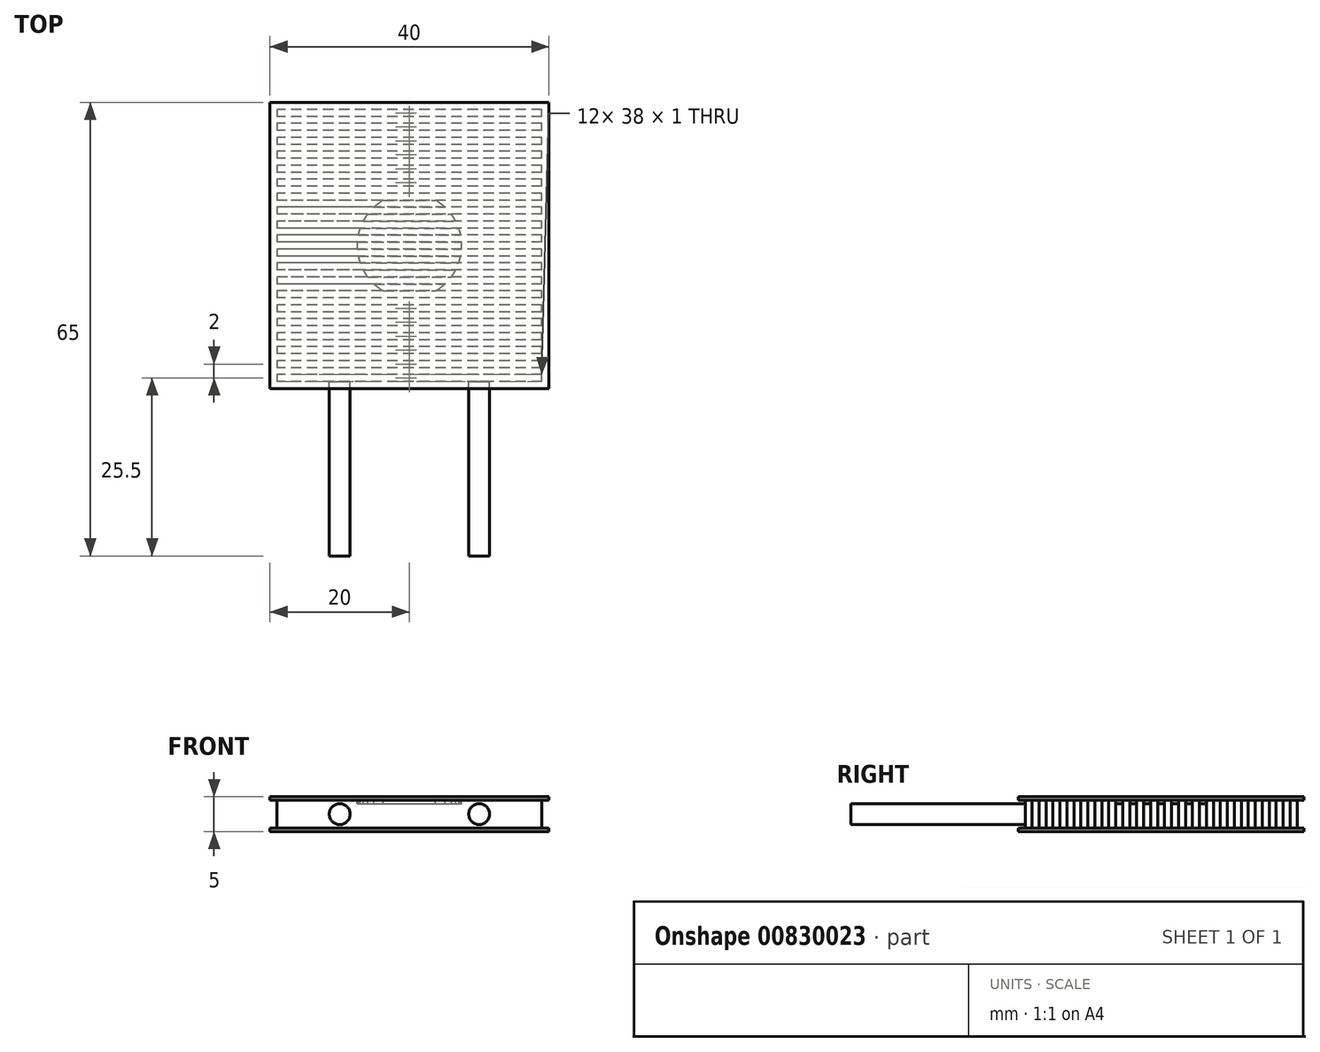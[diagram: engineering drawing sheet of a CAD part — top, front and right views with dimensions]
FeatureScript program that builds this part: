
annotation { "Feature Type Name" : "Feature", "Feature Type Description" : "" }
export const myFeature = defineFeature(function(context is Context, id is Id, definition is map)
    precondition{}
    {
        {
            var Q0;
            Q0=qCreatedBy(makeId("Top.planeOp"),FACE);
            var sketch = newSketch(context, id + "F0", { "sketchPlane" : qUnion([Q0])});
            skLineSegment(sketch, "E0.bottom", {"start": v(0, 0) * mm, "end": v(40, 0) * mm});
            skLineSegment(sketch, "E0.top", {"start": v(0, -41) * mm, "end": v(40, -41) * mm});
            skLineSegment(sketch, "E0.left", {"start": v(0, 0) * mm, "end": v(0, -41) * mm});
            skLineSegment(sketch, "E0.right", {"start": v(40, 0) * mm, "end": v(40, -41) * mm});
            skSolve(sketch);
        }
        {
            var Q0;
            Q0=makeQuery(id+"F0.imprint","IMPRINT",FACE,{"disambiguationData":[TD([[makeQuery(id+"F0.imprint","IMPRINT",EDGE,{"derivedFrom":sQuery(id+"F0.wireOp",EDGE,"E0.bottom")}),-1.0]])]});
            extrude(context, id + "F1", {"entities" : qUnion([Q0]), "depth" : 5 * mm, "offsetDistance" : 25 * mm});
        }
        {
            var Q0;
            Q0=makeQuery(id+"F1.opExtrude","SWEPT_FACE",FACE,{"disambiguationData":[OSD([sQuery(id+"F0.wireOp",EDGE,"E0.left")])]});
            var sketch = newSketch(context, id + "F2", { "sketchPlane" : qUnion([Q0])});
            skLineSegment(sketch, "E1.bottom", {"start": v(0, 4.5) * mm, "end": v(1, 4.5) * mm});
            skLineSegment(sketch, "E1.top", {"start": v(0, 0.5) * mm, "end": v(1, 0.5) * mm});
            skLineSegment(sketch, "E1.left", {"start": v(0, 4.5) * mm, "end": v(0, 0.5) * mm});
            skLineSegment(sketch, "E1.right", {"start": v(1, 4.5) * mm, "end": v(1, 0.5) * mm});
            skLineSegment(sketch, "E2.1.0.0", {"start": v(3, 4.5) * mm, "end": v(3, 0.5) * mm});
            skLineSegment(sketch, "E2.1.0.1", {"start": v(2, 4.5) * mm, "end": v(2, 0.5) * mm});
            skLineSegment(sketch, "E2.1.0.2", {"start": v(2, 4.5) * mm, "end": v(3, 4.5) * mm});
            skLineSegment(sketch, "E2.1.0.3", {"start": v(2, 0.5) * mm, "end": v(3, 0.5) * mm});
            skLineSegment(sketch, "E2.2.0.0", {"start": v(5, 4.5) * mm, "end": v(5, 0.5) * mm});
            skLineSegment(sketch, "E2.2.0.1", {"start": v(4, 4.5) * mm, "end": v(4, 0.5) * mm});
            skLineSegment(sketch, "E2.2.0.2", {"start": v(4, 4.5) * mm, "end": v(5, 4.5) * mm});
            skLineSegment(sketch, "E2.2.0.3", {"start": v(4, 0.5) * mm, "end": v(5, 0.5) * mm});
            skLineSegment(sketch, "E2.3.0.0", {"start": v(7, 4.5) * mm, "end": v(7, 0.5) * mm});
            skLineSegment(sketch, "E2.3.0.1", {"start": v(6, 4.5) * mm, "end": v(6, 0.5) * mm});
            skLineSegment(sketch, "E2.3.0.2", {"start": v(6, 4.5) * mm, "end": v(7, 4.5) * mm});
            skLineSegment(sketch, "E2.3.0.3", {"start": v(6, 0.5) * mm, "end": v(7, 0.5) * mm});
            skLineSegment(sketch, "E2.4.0.0", {"start": v(9, 4.5) * mm, "end": v(9, 0.5) * mm});
            skLineSegment(sketch, "E2.4.0.1", {"start": v(8, 4.5) * mm, "end": v(8, 0.5) * mm});
            skLineSegment(sketch, "E2.4.0.2", {"start": v(8, 4.5) * mm, "end": v(9, 4.5) * mm});
            skLineSegment(sketch, "E2.4.0.3", {"start": v(8, 0.5) * mm, "end": v(9, 0.5) * mm});
            skLineSegment(sketch, "E2.5.0.0", {"start": v(11, 4.5) * mm, "end": v(11, 0.5) * mm});
            skLineSegment(sketch, "E2.5.0.1", {"start": v(10, 4.5) * mm, "end": v(10, 0.5) * mm});
            skLineSegment(sketch, "E2.5.0.2", {"start": v(10, 4.5) * mm, "end": v(11, 4.5) * mm});
            skLineSegment(sketch, "E2.5.0.3", {"start": v(10, 0.5) * mm, "end": v(11, 0.5) * mm});
            skLineSegment(sketch, "E2.6.0.0", {"start": v(13, 4.5) * mm, "end": v(13, 0.5) * mm});
            skLineSegment(sketch, "E2.6.0.1", {"start": v(12, 4.5) * mm, "end": v(12, 0.5) * mm});
            skLineSegment(sketch, "E2.6.0.2", {"start": v(12, 4.5) * mm, "end": v(13, 4.5) * mm});
            skLineSegment(sketch, "E2.6.0.3", {"start": v(12, 0.5) * mm, "end": v(13, 0.5) * mm});
            skLineSegment(sketch, "E2.7.0.0", {"start": v(15, 4.5) * mm, "end": v(15, 0.5) * mm});
            skLineSegment(sketch, "E2.7.0.1", {"start": v(14, 4.5) * mm, "end": v(14, 0.5) * mm});
            skLineSegment(sketch, "E2.7.0.2", {"start": v(14, 4.5) * mm, "end": v(15, 4.5) * mm});
            skLineSegment(sketch, "E2.7.0.3", {"start": v(14, 0.5) * mm, "end": v(15, 0.5) * mm});
            skLineSegment(sketch, "E2.8.0.0", {"start": v(17, 4.5) * mm, "end": v(17, 0.5) * mm});
            skLineSegment(sketch, "E2.8.0.1", {"start": v(16, 4.5) * mm, "end": v(16, 0.5) * mm});
            skLineSegment(sketch, "E2.8.0.2", {"start": v(16, 4.5) * mm, "end": v(17, 4.5) * mm});
            skLineSegment(sketch, "E2.8.0.3", {"start": v(16, 0.5) * mm, "end": v(17, 0.5) * mm});
            skLineSegment(sketch, "E2.9.0.0", {"start": v(19, 4.5) * mm, "end": v(19, 0.5) * mm});
            skLineSegment(sketch, "E2.9.0.1", {"start": v(18, 4.5) * mm, "end": v(18, 0.5) * mm});
            skLineSegment(sketch, "E2.9.0.2", {"start": v(18, 4.5) * mm, "end": v(19, 4.5) * mm});
            skLineSegment(sketch, "E2.9.0.3", {"start": v(18, 0.5) * mm, "end": v(19, 0.5) * mm});
            skLineSegment(sketch, "E2.10.0.0", {"start": v(21, 4.5) * mm, "end": v(21, 0.5) * mm});
            skLineSegment(sketch, "E2.10.0.1", {"start": v(20, 4.5) * mm, "end": v(20, 0.5) * mm});
            skLineSegment(sketch, "E2.10.0.2", {"start": v(20, 4.5) * mm, "end": v(21, 4.5) * mm});
            skLineSegment(sketch, "E2.10.0.3", {"start": v(20, 0.5) * mm, "end": v(21, 0.5) * mm});
            skLineSegment(sketch, "E2.11.0.0", {"start": v(23, 4.5) * mm, "end": v(23, 0.5) * mm});
            skLineSegment(sketch, "E2.11.0.1", {"start": v(22, 4.5) * mm, "end": v(22, 0.5) * mm});
            skLineSegment(sketch, "E2.11.0.2", {"start": v(22, 4.5) * mm, "end": v(23, 4.5) * mm});
            skLineSegment(sketch, "E2.11.0.3", {"start": v(22, 0.5) * mm, "end": v(23, 0.5) * mm});
            skLineSegment(sketch, "E2.12.0.0", {"start": v(25, 4.5) * mm, "end": v(25, 0.5) * mm});
            skLineSegment(sketch, "E2.12.0.1", {"start": v(24, 4.5) * mm, "end": v(24, 0.5) * mm});
            skLineSegment(sketch, "E2.12.0.2", {"start": v(24, 4.5) * mm, "end": v(25, 4.5) * mm});
            skLineSegment(sketch, "E2.12.0.3", {"start": v(24, 0.5) * mm, "end": v(25, 0.5) * mm});
            skLineSegment(sketch, "E2.13.0.0", {"start": v(27, 4.5) * mm, "end": v(27, 0.5) * mm});
            skLineSegment(sketch, "E2.13.0.1", {"start": v(26, 4.5) * mm, "end": v(26, 0.5) * mm});
            skLineSegment(sketch, "E2.13.0.2", {"start": v(26, 4.5) * mm, "end": v(27, 4.5) * mm});
            skLineSegment(sketch, "E2.13.0.3", {"start": v(26, 0.5) * mm, "end": v(27, 0.5) * mm});
            skLineSegment(sketch, "E2.14.0.0", {"start": v(29, 4.5) * mm, "end": v(29, 0.5) * mm});
            skLineSegment(sketch, "E2.14.0.1", {"start": v(28, 4.5) * mm, "end": v(28, 0.5) * mm});
            skLineSegment(sketch, "E2.14.0.2", {"start": v(28, 4.5) * mm, "end": v(29, 4.5) * mm});
            skLineSegment(sketch, "E2.14.0.3", {"start": v(28, 0.5) * mm, "end": v(29, 0.5) * mm});
            skLineSegment(sketch, "E2.15.0.0", {"start": v(31, 4.5) * mm, "end": v(31, 0.5) * mm});
            skLineSegment(sketch, "E2.15.0.1", {"start": v(30, 4.5) * mm, "end": v(30, 0.5) * mm});
            skLineSegment(sketch, "E2.15.0.2", {"start": v(30, 4.5) * mm, "end": v(31, 4.5) * mm});
            skLineSegment(sketch, "E2.15.0.3", {"start": v(30, 0.5) * mm, "end": v(31, 0.5) * mm});
            skLineSegment(sketch, "E2.16.0.0", {"start": v(33, 4.5) * mm, "end": v(33, 0.5) * mm});
            skLineSegment(sketch, "E2.16.0.1", {"start": v(32, 4.5) * mm, "end": v(32, 0.5) * mm});
            skLineSegment(sketch, "E2.16.0.2", {"start": v(32, 4.5) * mm, "end": v(33, 4.5) * mm});
            skLineSegment(sketch, "E2.16.0.3", {"start": v(32, 0.5) * mm, "end": v(33, 0.5) * mm});
            skLineSegment(sketch, "E2.17.0.0", {"start": v(35, 4.5) * mm, "end": v(35, 0.5) * mm});
            skLineSegment(sketch, "E2.17.0.1", {"start": v(34, 4.5) * mm, "end": v(34, 0.5) * mm});
            skLineSegment(sketch, "E2.17.0.2", {"start": v(34, 4.5) * mm, "end": v(35, 4.5) * mm});
            skLineSegment(sketch, "E2.17.0.3", {"start": v(34, 0.5) * mm, "end": v(35, 0.5) * mm});
            skLineSegment(sketch, "E2.18.0.0", {"start": v(37, 4.5) * mm, "end": v(37, 0.5) * mm});
            skLineSegment(sketch, "E2.18.0.1", {"start": v(36, 4.5) * mm, "end": v(36, 0.5) * mm});
            skLineSegment(sketch, "E2.18.0.2", {"start": v(36, 4.5) * mm, "end": v(37, 4.5) * mm});
            skLineSegment(sketch, "E2.18.0.3", {"start": v(36, 0.5) * mm, "end": v(37, 0.5) * mm});
            skLineSegment(sketch, "E2.19.0.0", {"start": v(39, 4.5) * mm, "end": v(39, 0.5) * mm});
            skLineSegment(sketch, "E2.19.0.1", {"start": v(38, 4.5) * mm, "end": v(38, 0.5) * mm});
            skLineSegment(sketch, "E2.19.0.2", {"start": v(38, 4.5) * mm, "end": v(39, 4.5) * mm});
            skLineSegment(sketch, "E2.19.0.3", {"start": v(38, 0.5) * mm, "end": v(39, 0.5) * mm});
            skLineSegment(sketch, "E2.direction1", {"start": v(0, 0.5) * mm, "end": v(2, 0.5) * mm, "construction": true});
            skLineSegment(sketch, "E3.0.20.0", {"start": v(41, 4.5) * mm, "end": v(41, 0.5) * mm});
            skLineSegment(sketch, "E3.3.20.0", {"start": v(40, 4.5) * mm, "end": v(40, 0.5) * mm});
            skLineSegment(sketch, "E3.6.20.0", {"start": v(40, 4.5) * mm, "end": v(41, 4.5) * mm});
            skLineSegment(sketch, "E3.9.20.0", {"start": v(40, 0.5) * mm, "end": v(41, 0.5) * mm});
            skSolve(sketch);
        }
        {
            var Q0;
            Q0 = qSketchRegion(id + "F2", true);
            extrude(context, id + "F3", {"entities" : qUnion([Q0]), "operationType" : NewBodyOperationType.REMOVE, "endBound" : BoundingType.THROUGH_ALL, "oppositeDirection" : true, "depth" : 25 * mm, "offsetDistance" : 25 * mm});
        }
        {
            var Q0;
            Q0=makeQuery(id+"F1.opExtrude","SWEPT_FACE",FACE,{"disambiguationData":[OSD([sQuery(id+"F0.wireOp",EDGE,"E0.left")])]});
            var sketch = newSketch(context, id + "F4", { "sketchPlane" : qUnion([Q0])});
            skPoint(sketch, "E4.oppositeSnap0", {"position": v(41, 0.25) * mm});
            skLineSegment(sketch, "E4.bottom", {"start": v(1, 4.5) * mm, "end": v(41, 4.5) * mm});
            skLineSegment(sketch, "E4.top", {"start": v(1, 0.5) * mm, "end": v(41, 0.5) * mm});
            skLineSegment(sketch, "E4.left", {"start": v(1, 4.5) * mm, "end": v(1, 0.5) * mm});
            skLineSegment(sketch, "E4.right", {"start": v(41, 4.5) * mm, "end": v(41, 0.5) * mm});
            skSolve(sketch);
        }
        {
            var Q0;
            Q0 = qSketchRegion(id + "F4", true);
            extrude(context, id + "F5", {"entities" : qUnion([Q0]), "operationType" : NewBodyOperationType.REMOVE, "oppositeDirection" : true, "depth" : 1 * mm, "offsetDistance" : 25 * mm});
        }
        {
            var Q0;
            Q0=makeQuery(id+"F1.opExtrude","SWEPT_FACE",FACE,{"disambiguationData":[OSD([sQuery(id+"F0.wireOp",EDGE,"E0.right")])]});
            var sketch = newSketch(context, id + "F6", { "sketchPlane" : qUnion([Q0])});
            skLineSegment(sketch, "E5.bottom", {"start": v(-1, 4.5) * mm, "end": v(-41, 4.5) * mm});
            skLineSegment(sketch, "E5.top", {"start": v(-1, 0.5) * mm, "end": v(-41, 0.5) * mm});
            skLineSegment(sketch, "E5.left", {"start": v(-1, 4.5) * mm, "end": v(-1, 0.5) * mm});
            skLineSegment(sketch, "E5.right", {"start": v(-41, 4.5) * mm, "end": v(-41, 0.5) * mm});
            skSolve(sketch);
        }
        {
            var Q0;
            Q0 = qSketchRegion(id + "F6", true);
            extrude(context, id + "F7", {"entities" : qUnion([Q0]), "operationType" : NewBodyOperationType.REMOVE, "oppositeDirection" : true, "depth" : 1 * mm, "offsetDistance" : 25 * mm});
        }
        {
            var Q0;
            Q0=makeQuery(id+"F3.boolean.opBoolean","COPY",FACE,{"derivedFrom":makeQuery(id+"F3.opExtrude","SWEPT_FACE",FACE,{"disambiguationData":[OSD([sQuery(id+"F2.wireOp",EDGE,"E3.3.20.0")])]})});
            var sketch = newSketch(context, id + "F8", { "sketchPlane" : qUnion([Q0])});
            skCircle(sketch, "E6", {"center": v(10, 2.5) * mm, "radius": 1.5 * mm});
            skCircle(sketch, "E7", {"center": v(30, 2.5) * mm, "radius": 1.5 * mm});
            skSolve(sketch);
        }
        {
            var Q0;
            Q0=makeQuery(id+"F8.imprint","IMPRINT",FACE,{"disambiguationData":[TD([[makeQuery(id+"F8.imprint","IMPRINT",EDGE,{"derivedFrom":sQuery(id+"F8.wireOp",EDGE,"E6")}),1.0]])]});
            var Q1;
            Q1=makeQuery(id+"F8.imprint","IMPRINT",FACE,{"disambiguationData":[TD([[makeQuery(id+"F8.imprint","IMPRINT",EDGE,{"derivedFrom":sQuery(id+"F8.wireOp",EDGE,"E7")}),1.0]])]});
            extrude(context, id + "F9", {"entities" : qUnion([Q0, Q1]), "operationType" : NewBodyOperationType.ADD, "depth" : 25 * mm, "offsetDistance" : 25 * mm});
        }
        {
            var Q0;
            Q0=makeQuery(id+"F1.opExtrude","CAP_FACE",FACE,{"disambiguationData":[OSD([sQuery(id+"F0.wireOp",EDGE,"E0.bottom"),sQuery(id+"F0.wireOp",EDGE,"E0.top"),sQuery(id+"F0.wireOp",EDGE,"E0.left"),sQuery(id+"F0.wireOp",EDGE,"E0.right")])],"isStart":false});
            var sketch = newSketch(context, id + "F10", { "sketchPlane" : qUnion([Q0])});
            skCircle(sketch, "E8", {"center": v(20, -20.5) * mm, "radius": 7.5 * mm});
            skSolve(sketch);
        }
        {
            var Q0;
            Q0=makeQuery(id+"F10.imprint","IMPRINT",FACE,{"disambiguationData":[TD([[makeQuery(id+"F10.imprint","IMPRINT",EDGE,{"derivedFrom":sQuery(id+"F10.wireOp",EDGE,"E8")}),1.0]])]});
            extrude(context, id + "F11", {"entities" : qUnion([Q0]), "operationType" : NewBodyOperationType.ADD, "oppositeDirection" : true, "depth" : 1 * mm, "offsetDistance" : 25 * mm});
        }
    });
